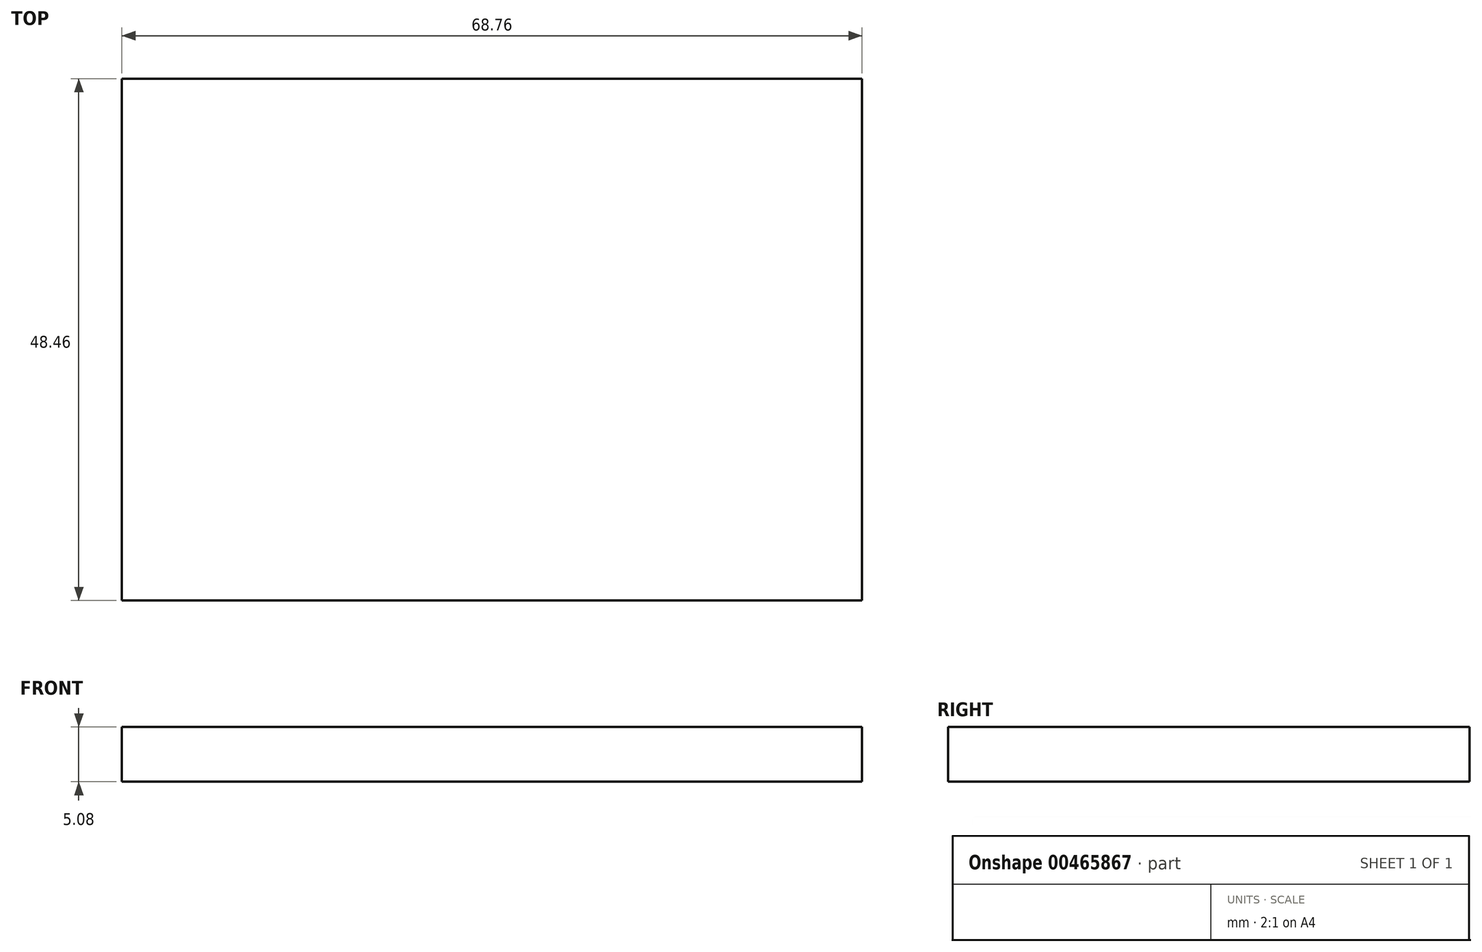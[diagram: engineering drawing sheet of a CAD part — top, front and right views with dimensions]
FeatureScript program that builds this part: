
annotation { "Feature Type Name" : "Feature", "Feature Type Description" : "" }
export const myFeature = defineFeature(function(context is Context, id is Id, definition is map)
    precondition{}
    {
        {
            var Q0;
            Q0=qCreatedBy(makeId("Top.planeOp"),FACE);
            var sketch = newSketch(context, id + "F0", { "sketchPlane" : qUnion([Q0])});
            skLineSegment(sketch, "E0.bottom", {"start": v(0, 0) * mm, "end": v(68.76, 0) * mm});
            skLineSegment(sketch, "E0.top", {"start": v(0, 48.46) * mm, "end": v(68.76, 48.46) * mm});
            skLineSegment(sketch, "E0.left", {"start": v(0, 0) * mm, "end": v(0, 48.46) * mm});
            skLineSegment(sketch, "E0.right", {"start": v(68.76, 0) * mm, "end": v(68.76, 48.46) * mm});
            skSolve(sketch);
        }
        {
            var Q0;
            Q0=makeQuery(id+"F0.imprint","IMPRINT",FACE,{"disambiguationData":[TD([[makeQuery(id+"F0.imprint","IMPRINT",EDGE,{"derivedFrom":sQuery(id+"F0.wireOp",EDGE,"E0.bottom")}),1.0]])]});
            extrude(context, id + "F1", {"entities" : qUnion([Q0]), "depth" : 5.08 * mm});
        }
    });
